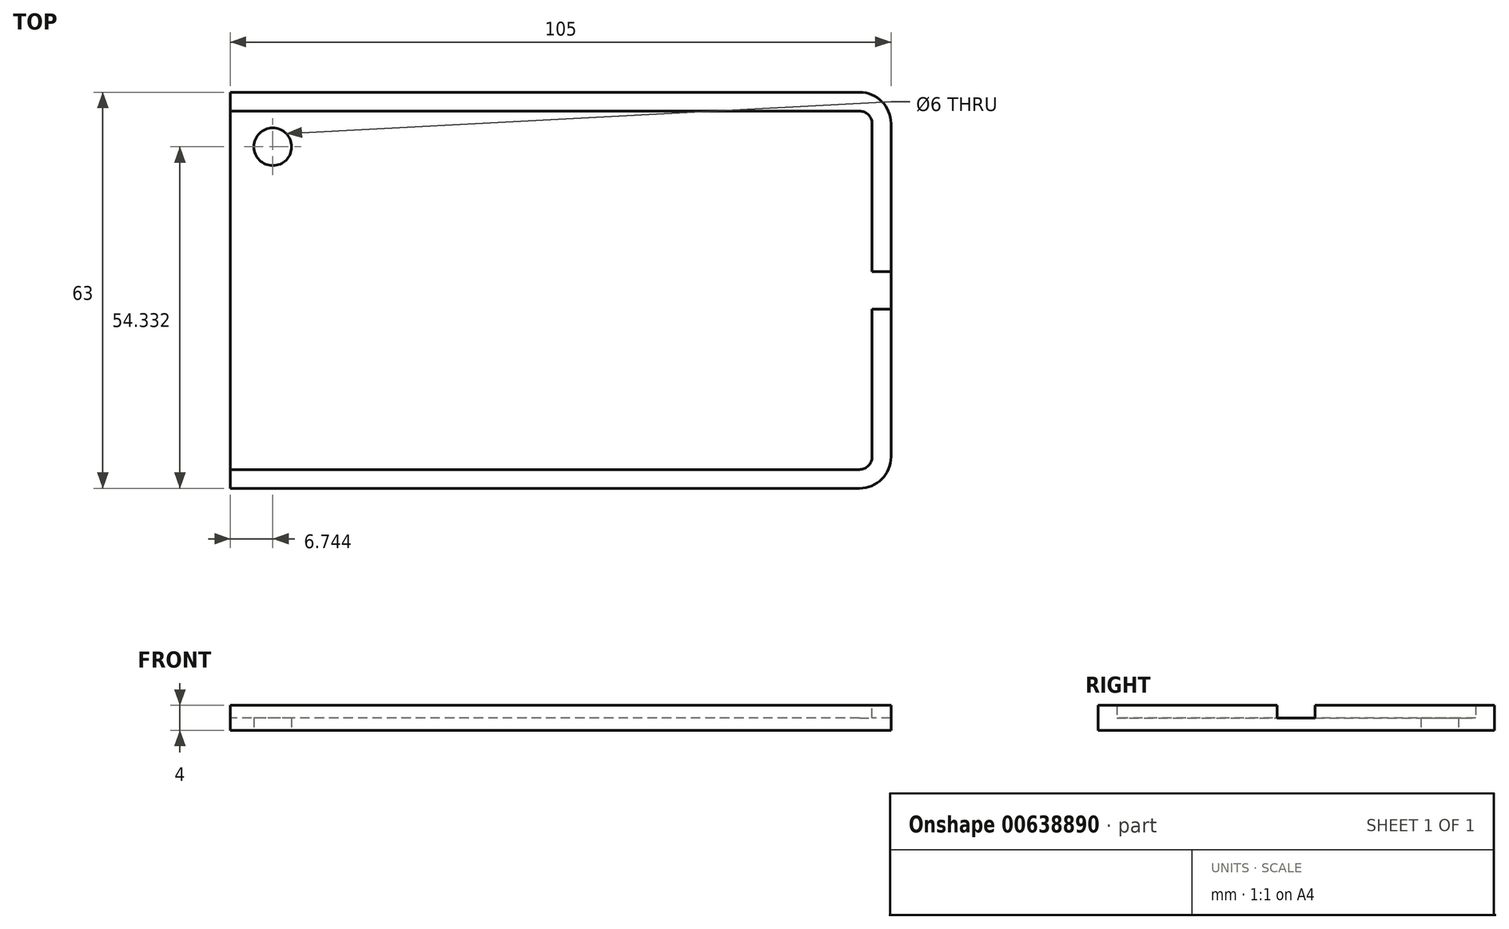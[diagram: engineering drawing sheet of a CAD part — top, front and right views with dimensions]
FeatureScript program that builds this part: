
annotation { "Feature Type Name" : "Feature", "Feature Type Description" : "" }
export const myFeature = defineFeature(function(context is Context, id is Id, definition is map)
    precondition{}
    {
        {
            var Q0;
            Q0=qCreatedBy(makeId("Top.planeOp"),FACE);
            var sketch = newSketch(context, id + "F0", { "sketchPlane" : qUnion([Q0])});
            skLineSegment(sketch, "E0.bottom", {"start": v(43, -27.5) * mm, "end": v(-43, -27.5) * mm});
            skLineSegment(sketch, "E0.top", {"start": v(43, 27.5) * mm, "end": v(-43, 27.5) * mm});
            skLineSegment(sketch, "E0.left", {"start": v(44, -26.5) * mm, "end": v(44, 26.5) * mm});
            skLineSegment(sketch, "E0.right", {"start": v(-44, -26.5) * mm, "end": v(-44, 26.5) * mm});
            skPoint(sketch, "E0.middle", {"position": v(0, 0) * mm});
            skPoint(sketch, "E1.visualSharp", {"position": v(-44, 27.5) * mm});
            skArc(sketch, "E1.filletArc", {"start": v(-43, 27.5) * mm, "mid": v(-43.7, 27.2) * mm, "end": v(-44, 26.5) * mm});
            skPoint(sketch, "E2.visualSharp", {"position": v(-44, -27.5) * mm});
            skArc(sketch, "E2.filletArc", {"start": v(-44, -26.5) * mm, "mid": v(-43.7, -27.2) * mm, "end": v(-43, -27.5) * mm});
            skPoint(sketch, "E3.visualSharp", {"position": v(44, -27.5) * mm});
            skArc(sketch, "E3.filletArc", {"start": v(43, -27.5) * mm, "mid": v(43.7, -27.2) * mm, "end": v(44, -26.5) * mm});
            skPoint(sketch, "E4.visualSharp", {"position": v(44, 27.5) * mm});
            skArc(sketch, "E4.filletArc", {"start": v(44, 26.5) * mm, "mid": v(43.7, 27.2) * mm, "end": v(43, 27.5) * mm});
            skArc(sketch, "E5.0", {"start": v(43, -28.5) * mm, "mid": v(44.41, -27.91) * mm, "end": v(45, -26.5) * mm});
            skLineSegment(sketch, "E5.1", {"start": v(45, -26.5) * mm, "end": v(45, 26.5) * mm});
            skLineSegment(sketch, "E5.2", {"start": v(43, -28.5) * mm, "end": v(-57, -28.5) * mm});
            skArc(sketch, "E5.3", {"start": v(45, 26.5) * mm, "mid": v(44.41, 27.91) * mm, "end": v(43, 28.5) * mm});
            skLineSegment(sketch, "E5.7", {"start": v(43, 28.5) * mm, "end": v(-57, 28.5) * mm});
            skArc(sketch, "E6.0", {"start": v(48, 26.5) * mm, "mid": v(46.54, 30.04) * mm, "end": v(43, 31.5) * mm});
            skLineSegment(sketch, "E6.1", {"start": v(48, -26.5) * mm, "end": v(48, 26.5) * mm});
            skLineSegment(sketch, "E6.2", {"start": v(43, 31.5) * mm, "end": v(-57, 31.5) * mm});
            skArc(sketch, "E6.3", {"start": v(43, -31.5) * mm, "mid": v(46.54, -30.04) * mm, "end": v(48, -26.5) * mm});
            skLineSegment(sketch, "E6.7", {"start": v(43, -31.5) * mm, "end": v(-57, -31.5) * mm});
            skLineSegment(sketch, "E7", {"start": v(-45, 28.5) * mm, "end": v(-45, -28.5) * mm, "construction": true});
            skLineSegment(sketch, "E8", {"start": v(-47, 28.5) * mm, "end": v(-47, -28.5) * mm, "construction": true});
            skPoint(sketch, "E9", {"position": v(-47, 28.5) * mm});
            skCircle(sketch, "E10", {"center": v(-50.26, 22.83) * mm, "radius": 3 * mm});
            skLineSegment(sketch, "E11", {"start": v(-57, 31.5) * mm, "end": v(-57, -31.5) * mm});
            skSolve(sketch);
        }
        {
            var Q0;
            Q0=makeQuery(id+"F0.imprint","IMPRINT",FACE,{"disambiguationData":[TD([[makeQuery(id+"F0.imprint","IMPRINT",EDGE,{"derivedFrom":sQuery(id+"F0.wireOp",EDGE,"E10")}),1.0]])]});
            var Q1;
            Q1=makeQuery(id+"F0.imprint","IMPRINT",FACE,{"disambiguationData":[TD([[makeQuery(id+"F0.imprint","IMPRINT",EDGE,{"derivedFrom":sQuery(id+"F0.wireOp",EDGE,"E0.bottom")}),1.0]])]});
            var Q2;
            Q2=makeQuery(id+"F0.imprint","IMPRINT",FACE,{"disambiguationData":[TD([[makeQuery(id+"F0.imprint","IMPRINT",EDGE,{"derivedFrom":sQuery(id+"F0.wireOp",EDGE,"E0.bottom")}),-1.0]])]});
            extrude(context, id + "F1", {"entities" : qUnion([Q0, Q1, Q2]), "depth" : 2 * mm, "offsetDistance" : 25 * mm});
        }
        {
            var Q0;
            Q0=makeQuery(id+"F0.imprint","IMPRINT",FACE,{"disambiguationData":[TD([[makeQuery(id+"F0.imprint","IMPRINT",EDGE,{"derivedFrom":sQuery(id+"F0.wireOp",EDGE,"E5.0")}),-1.0]])]});
            extrude(context, id + "F2", {"entities" : qUnion([Q0]), "operationType" : NewBodyOperationType.ADD, "depth" : 4 * mm, "offsetDistance" : 25 * mm});
        }
        {
            var Q0;
            Q0=makeQuery(id+"F2.opExtrude","CAP_FACE",FACE,{"disambiguationData":[OSD([sQuery(id+"F0.wireOp",EDGE,"E5.0"),sQuery(id+"F0.wireOp",EDGE,"E5.1"),sQuery(id+"F0.wireOp",EDGE,"E5.2"),sQuery(id+"F0.wireOp",EDGE,"E5.3"),sQuery(id+"F0.wireOp",EDGE,"E5.7"),sQuery(id+"F0.wireOp",EDGE,"E6.0"),sQuery(id+"F0.wireOp",EDGE,"E6.1"),sQuery(id+"F0.wireOp",EDGE,"E6.2"),sQuery(id+"F0.wireOp",EDGE,"E6.3"),sQuery(id+"F0.wireOp",EDGE,"E6.7"),sQuery(id+"F0.wireOp",EDGE,"E11")])],"isStart":false});
            var sketch = newSketch(context, id + "F3", { "sketchPlane" : qUnion([Q0])});
            skLineSegment(sketch, "E12", {"start": v(42.83, 0) * mm, "end": v(50.28, 0) * mm, "construction": true});
            skPoint(sketch, "E12.endSnap0", {"position": v(45, 0) * mm});
            skPoint(sketch, "E13", {"position": v(48, 0) * mm});
            skLineSegment(sketch, "E14", {"start": v(45, 0) * mm, "end": v(45, 3) * mm});
            skLineSegment(sketch, "E15", {"start": v(45, 3) * mm, "end": v(48, 3) * mm});
            skLineSegment(sketch, "E16", {"start": v(48, 3) * mm, "end": v(48, 0) * mm});
            skLineSegment(sketch, "E17", {"start": v(48, 0) * mm, "end": v(48, -3) * mm});
            skLineSegment(sketch, "E18", {"start": v(48, -3) * mm, "end": v(45, -3) * mm});
            skLineSegment(sketch, "E19", {"start": v(45, -3) * mm, "end": v(45, 0) * mm});
            skSolve(sketch);
        }
        {
            var Q0;
            Q0=makeQuery(id+"F3.imprint","IMPRINT",FACE,{"disambiguationData":[TD([[makeQuery(id+"F3.imprint","IMPRINT",EDGE,{"derivedFrom":sQuery(id+"F3.wireOp",EDGE,"E14")}),-1.0]])]});
            extrude(context, id + "F4", {"entities" : qUnion([Q0]), "operationType" : NewBodyOperationType.REMOVE, "oppositeDirection" : true, "depth" : 2 * mm, "offsetDistance" : 25 * mm});
        }
        {
            var Q0;
            Q0=makeQuery(id+"F0.imprint","IMPRINT",FACE,{"disambiguationData":[TD([[makeQuery(id+"F0.imprint","IMPRINT",EDGE,{"derivedFrom":sQuery(id+"F0.wireOp",EDGE,"E10")}),1.0]])]});
            extrude(context, id + "F5", {"entities" : qUnion([Q0]), "operationType" : NewBodyOperationType.REMOVE, "oppositeDirection" : true, "depth" : -3 * mm, "offsetDistance" : 25 * mm});
        }
    });
